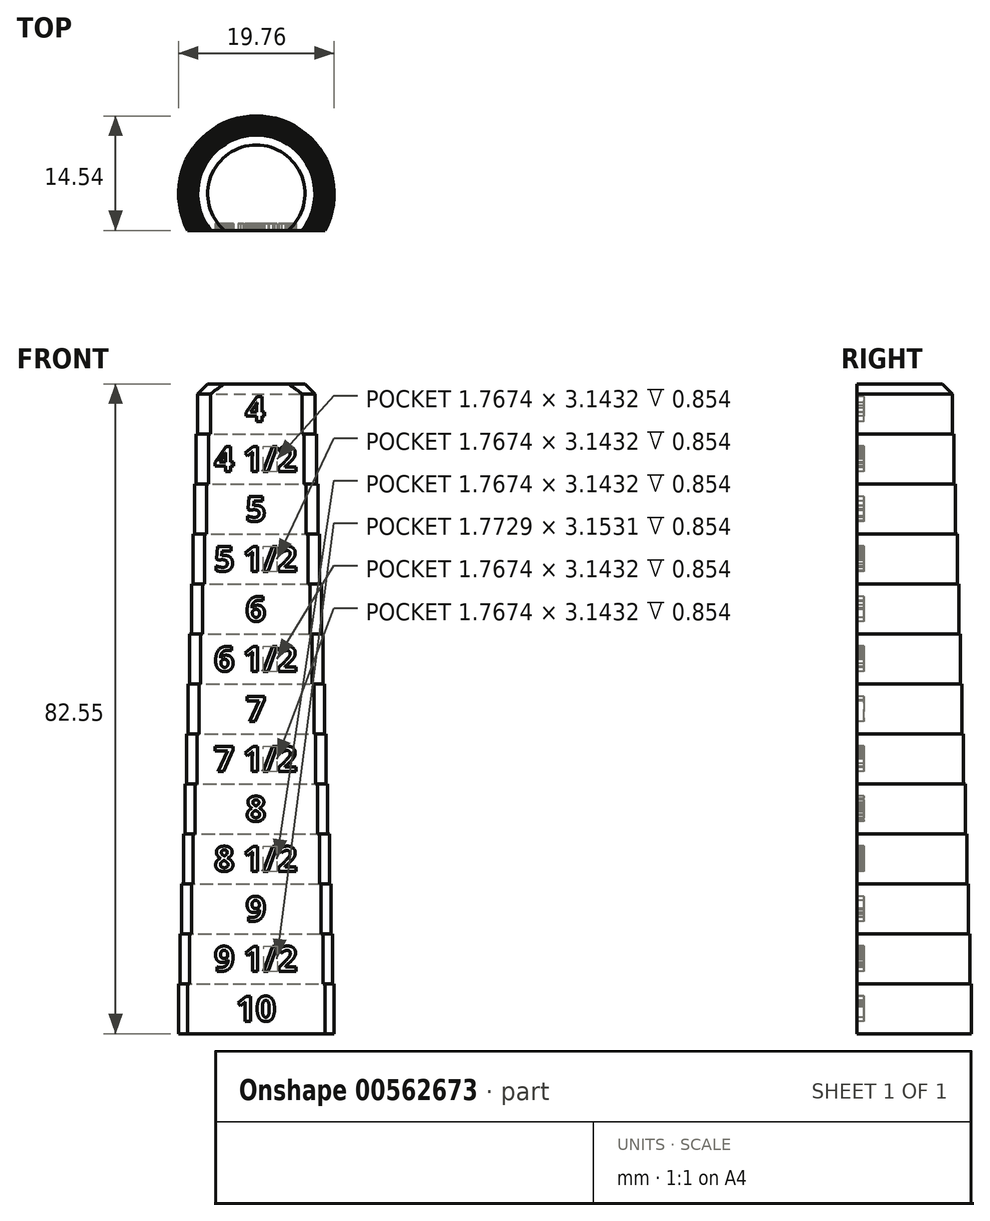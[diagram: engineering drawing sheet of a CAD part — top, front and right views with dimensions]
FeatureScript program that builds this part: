
annotation { "Feature Type Name" : "Feature", "Feature Type Description" : "" }
export const myFeature = defineFeature(function(context is Context, id is Id, definition is map)
    precondition{}
    {
        {
            var Q0;
            Q0=qCreatedBy(makeId("Front.planeOp"),FACE);
            var sketch = newSketch(context, id + "F0", { "sketchPlane" : qUnion([Q0])});
            skLineSegment(sketch, "E0.bottom", {"start": v(0, 0) * mm, "end": v(9.88, 0) * mm});
            skLineSegment(sketch, "E0.top", {"start": v(0, 140.21) * mm, "end": v(9.88, 140.21) * mm});
            skLineSegment(sketch, "E0.left", {"start": v(0, 0) * mm, "end": v(0, 82.55) * mm});
            skLineSegment(sketch, "E0.right", {"start": v(9.88, 0) * mm, "end": v(9.88, 6.35) * mm});
            skLineSegment(sketch, "E1.bottom", {"start": v(0, 6.35) * mm, "end": v(9.68, 6.35) * mm});
            skLineSegment(sketch, "E1.top", {"start": v(0, 12.7) * mm, "end": v(9.68, 12.7) * mm});
            skLineSegment(sketch, "E1.left", {"start": v(0, 6.35) * mm, "end": v(0, 12.7) * mm});
            skLineSegment(sketch, "E1.right", {"start": v(9.68, 6.35) * mm, "end": v(9.68, 12.7) * mm});
            skLineSegment(sketch, "E2.bottom", {"start": v(0, 12.7) * mm, "end": v(9.47, 12.7) * mm});
            skLineSegment(sketch, "E2.top", {"start": v(0, 19.05) * mm, "end": v(9.47, 19.05) * mm});
            skLineSegment(sketch, "E2.left", {"start": v(0, 12.7) * mm, "end": v(0, 19.05) * mm});
            skLineSegment(sketch, "E2.right", {"start": v(9.47, 12.7) * mm, "end": v(9.47, 19.05) * mm});
            skLineSegment(sketch, "E3.bottom", {"start": v(0, 19.05) * mm, "end": v(9.27, 19.05) * mm});
            skLineSegment(sketch, "E3.top", {"start": v(0, 25.4) * mm, "end": v(9.27, 25.4) * mm});
            skLineSegment(sketch, "E3.left", {"start": v(0, 19.05) * mm, "end": v(0, 25.4) * mm});
            skLineSegment(sketch, "E3.right", {"start": v(9.27, 19.05) * mm, "end": v(9.27, 25.4) * mm});
            skLineSegment(sketch, "E4.bottom", {"start": v(0, 25.4) * mm, "end": v(9.07, 25.4) * mm});
            skLineSegment(sketch, "E4.top", {"start": v(0, 31.75) * mm, "end": v(9.07, 31.75) * mm});
            skLineSegment(sketch, "E4.left", {"start": v(0, 25.4) * mm, "end": v(0, 31.75) * mm});
            skLineSegment(sketch, "E4.right", {"start": v(9.07, 25.4) * mm, "end": v(9.07, 31.75) * mm});
            skLineSegment(sketch, "E5.bottom", {"start": v(0, 31.75) * mm, "end": v(8.86, 31.75) * mm});
            skLineSegment(sketch, "E5.top", {"start": v(0, 38.1) * mm, "end": v(8.86, 38.1) * mm});
            skLineSegment(sketch, "E5.left", {"start": v(0, 31.75) * mm, "end": v(0, 38.1) * mm});
            skLineSegment(sketch, "E5.right", {"start": v(8.86, 31.75) * mm, "end": v(8.86, 38.1) * mm});
            skLineSegment(sketch, "E6.bottom", {"start": v(0, 38.1) * mm, "end": v(8.66, 38.1) * mm});
            skLineSegment(sketch, "E6.top", {"start": v(0, 44.45) * mm, "end": v(8.66, 44.45) * mm});
            skLineSegment(sketch, "E6.left", {"start": v(0, 38.1) * mm, "end": v(0, 44.45) * mm});
            skLineSegment(sketch, "E6.right", {"start": v(8.66, 38.1) * mm, "end": v(8.66, 44.45) * mm});
            skLineSegment(sketch, "E7.bottom", {"start": v(0, 44.45) * mm, "end": v(8.46, 44.45) * mm});
            skLineSegment(sketch, "E7.top", {"start": v(0, 50.8) * mm, "end": v(8.46, 50.8) * mm});
            skLineSegment(sketch, "E7.left", {"start": v(0, 44.45) * mm, "end": v(0, 50.8) * mm});
            skLineSegment(sketch, "E7.right", {"start": v(8.46, 44.45) * mm, "end": v(8.46, 50.8) * mm});
            skLineSegment(sketch, "E8", {"start": v(9.68, 6.35) * mm, "end": v(9.88, 6.35) * mm});
            skLineSegment(sketch, "E9.bottom", {"start": v(0, 50.8) * mm, "end": v(8.25, 50.8) * mm});
            skLineSegment(sketch, "E9.top", {"start": v(0, 57.15) * mm, "end": v(8.25, 57.15) * mm});
            skLineSegment(sketch, "E9.left", {"start": v(0, 50.8) * mm, "end": v(0, 57.15) * mm});
            skLineSegment(sketch, "E9.right", {"start": v(8.25, 50.8) * mm, "end": v(8.25, 57.15) * mm});
            skLineSegment(sketch, "E10.bottom", {"start": v(0, 57.15) * mm, "end": v(8.05, 57.15) * mm});
            skLineSegment(sketch, "E10.top", {"start": v(0, 63.5) * mm, "end": v(8.05, 63.5) * mm});
            skLineSegment(sketch, "E10.left", {"start": v(0, 57.15) * mm, "end": v(0, 63.5) * mm});
            skLineSegment(sketch, "E10.right", {"start": v(8.05, 57.15) * mm, "end": v(8.05, 63.5) * mm});
            skLineSegment(sketch, "E11.bottom", {"start": v(0, 63.5) * mm, "end": v(7.85, 63.5) * mm});
            skLineSegment(sketch, "E11.top", {"start": v(0, 69.85) * mm, "end": v(7.85, 69.85) * mm});
            skLineSegment(sketch, "E11.left", {"start": v(0, 63.5) * mm, "end": v(0, 69.85) * mm});
            skLineSegment(sketch, "E11.right", {"start": v(7.85, 63.5) * mm, "end": v(7.85, 69.85) * mm});
            skLineSegment(sketch, "E12.bottom", {"start": v(0, 69.85) * mm, "end": v(7.65, 69.85) * mm});
            skLineSegment(sketch, "E12.top", {"start": v(0, 76.2) * mm, "end": v(7.65, 76.2) * mm});
            skLineSegment(sketch, "E12.left", {"start": v(0, 69.85) * mm, "end": v(0, 76.2) * mm});
            skLineSegment(sketch, "E12.right", {"start": v(7.65, 69.85) * mm, "end": v(7.65, 76.2) * mm});
            skLineSegment(sketch, "E13.bottom", {"start": v(0, 76.2) * mm, "end": v(7.44, 76.2) * mm});
            skLineSegment(sketch, "E13.top", {"start": v(0, 82.55) * mm, "end": v(7.44, 82.55) * mm});
            skLineSegment(sketch, "E13.left", {"start": v(0, 76.2) * mm, "end": v(0, 82.55) * mm});
            skLineSegment(sketch, "E13.right", {"start": v(7.44, 76.2) * mm, "end": v(7.44, 82.55) * mm});
            skSolve(sketch);
        }
        {
            var Q0;
            Q0 = qSketchRegion(id + "F0", true);
            var Q1;
            Q1=sQuery(id+"F0.wireOp",EDGE,"E0.left");
            revolve(context, id + "F1", {"entities" : qUnion([Q0]), "axis" : qUnion([Q1]), "revolveType" : RevolveType.FULL});
        }
        {
            var Q0;
            Q0=makeQuery(id+"F1.opRevolve","SWEPT_EDGE",EDGE,{"disambiguationData":[OSD([sQuery(id+"F0.wireOp",EDGE,"E13.top"),sQuery(id+"F0.wireOp",EDGE,"E13.right")])]});
            chamfer(context, id + "F2", {"entities" : qUnion([Q0]), "width" : 1.27 * mm, "tangentPropagation" : true});
        }
        {
            var Q0;
            Q0=qCreatedBy(makeId("Front.planeOp"),FACE);
            cPlane(context, id + "F3", {"entities" : qUnion([Q0]), "cplaneType" : CPlaneType.OFFSET, "offset" : 10.16 * mm, "width" : 152.4 * mm, "height" : 152.4 * mm});
        }
        {
            var Q0;
            Q0=qCreatedBy(id+"F3.planeOp",FACE);
            var sketch = newSketch(context, id + "F4", { "sketchPlane" : qUnion([Q0])});
            skText(sketch, "E14", { "text": "10", "fontName": "OpenSans-Bold.ttf"});
            skText(sketch, "E15", { "text": "9 1/2", "fontName": "OpenSans-Bold.ttf"});
            skText(sketch, "E16", { "text": "9", "fontName": "OpenSans-Bold.ttf"});
            skText(sketch, "E17", { "text": "8 1/2", "fontName": "OpenSans-Bold.ttf"});
            skText(sketch, "E18", { "text": "8", "fontName": "OpenSans-Bold.ttf"});
            skText(sketch, "E19", { "text": "7 1/2", "fontName": "OpenSans-Bold.ttf"});
            skText(sketch, "E20", { "text": "7", "fontName": "OpenSans-Bold.ttf"});
            skText(sketch, "E21", { "text": "6 1/2", "fontName": "OpenSans-Bold.ttf"});
            skText(sketch, "E22", { "text": "6", "fontName": "OpenSans-Bold.ttf"});
            skText(sketch, "E23", { "text": "5 1/2", "fontName": "OpenSans-Bold.ttf"});
            skText(sketch, "E24", { "text": "5", "fontName": "OpenSans-Bold.ttf"});
            skText(sketch, "E25", { "text": "4 1/2", "fontName": "OpenSans-Bold.ttf"});
            skText(sketch, "E26", { "text": "4", "fontName": "OpenSans-Bold.ttf"});
            const initialGuessF4  = {"E14": [-0.00258, 0.00159, 1, 0, 0.00318], "E15": [-0.00533, 0.00794, 1, 0, 0.00318], "E16": [-0.00132, 0.01429, 1, 0, 0.00317], "E17": [-0.00533, 0.02064, 1, 0, 0.00317], "E18": [-0.00132, 0.02699, 1, 0, 0.00318], "E19": [-0.00533, 0.03334, 1, 0, 0.00317], "E20": [-0.00133, 0.03969, 1, 0, 0.00317], "E21": [-0.00533, 0.04604, 1, 0, 0.00317], "E22": [-0.00133, 0.05239, 1, 0, 0.00317], "E23": [-0.00533, 0.05874, 1, 0, 0.00317], "E24": [-0.0013, 0.06509, 1, 0, 0.00317], "E25": [-0.00533, 0.07144, 1, 0, 0.00317], "E26": [-0.00137, 0.07779, 1, 0, 0.00317]};
            skSetInitialGuess(sketch, initialGuessF4);
            skSolve(sketch);
        }
        {
            var Q0;
            Q0=makeQuery(id+"F1.opRevolve","SWEPT_FACE",FACE,{"disambiguationData":[OSD([sQuery(id+"F0.wireOp",EDGE,"E13.top")])]});
            var sketch = newSketch(context, id + "F5", { "sketchPlane" : qUnion([Q0])});
            skLineSegment(sketch, "E27.bottom", {"start": v(-12.7, -4.66) * mm, "end": v(12.7, -4.66) * mm});
            skLineSegment(sketch, "E27.top", {"start": v(-12.7, -10.12) * mm, "end": v(12.7, -10.12) * mm});
            skLineSegment(sketch, "E27.left", {"start": v(-12.7, -4.66) * mm, "end": v(-12.7, -10.12) * mm});
            skLineSegment(sketch, "E27.right", {"start": v(12.7, -4.66) * mm, "end": v(12.7, -10.12) * mm});
            skSolve(sketch);
        }
        {
            var Q0;
            Q0=makeQuery(id+"F5.imprint","IMPRINT",FACE,{"disambiguationData":[TD([[makeQuery(id+"F5.imprint","IMPRINT",EDGE,{"derivedFrom":sQuery(id+"F5.wireOp",EDGE,"E27.top")}),1.0]])]});
            var Q1;
            {var subQ0=sQuery(id+"F5.wireOp",EDGE,"E27.bottom");var subQ1=sQuery(id+"F0.wireOp",EDGE,"E13.top");var subQ2=makeQuery(id+"F2.opChamfer","BLEND_EDGE",EDGE,{"blendedFrom":[makeQuery(id+"F1.opRevolve","SWEPT_EDGE",EDGE,{"disambiguationData":[OSD([subQ1,sQuery(id+"F0.wireOp",EDGE,"E13.right")])]}),makeQuery(id+"F1.opRevolve","SWEPT_FACE",FACE,{"disambiguationData":[OSD([subQ1])]})],"blendedInto":[makeQuery(id+"F1.opRevolve","SWEPT_FACE",FACE,{"disambiguationData":[OSD([subQ1])]})]});var subQ3=makeQuery(id+"F5.imprint","INTERSECT",VERTEX,{"disambiguationData":[OD(0.0)],"derivedFrom":[subQ2,subQ0]});Q1=makeQuery(id+"F5.imprint","IMPRINT",FACE,{"disambiguationData":[TD([[makeQuery(id+"F5.imprint","IMPRINT",EDGE,{"disambiguationData":[TD([[subQ3,-1.0]])],"derivedFrom":subQ0}),-1.0]])]});}
            extrude(context, id + "F6", {"entities" : qUnion([Q0, Q1]), "operationType" : NewBodyOperationType.REMOVE, "endBound" : BoundingType.THROUGH_ALL, "oppositeDirection" : true, "depth" : 25.4 * mm, "offsetDistance" : 25.4 * mm});
        }
        {
            var Q0;
            Q0 = qSketchRegion(id + "F4", true);
            extrude(context, id + "F7", {"entities" : qUnion([Q0]), "operationType" : NewBodyOperationType.REMOVE, "oppositeDirection" : true, "depth" : 6.35 * mm, "offsetDistance" : 25.4 * mm});
        }
    });
